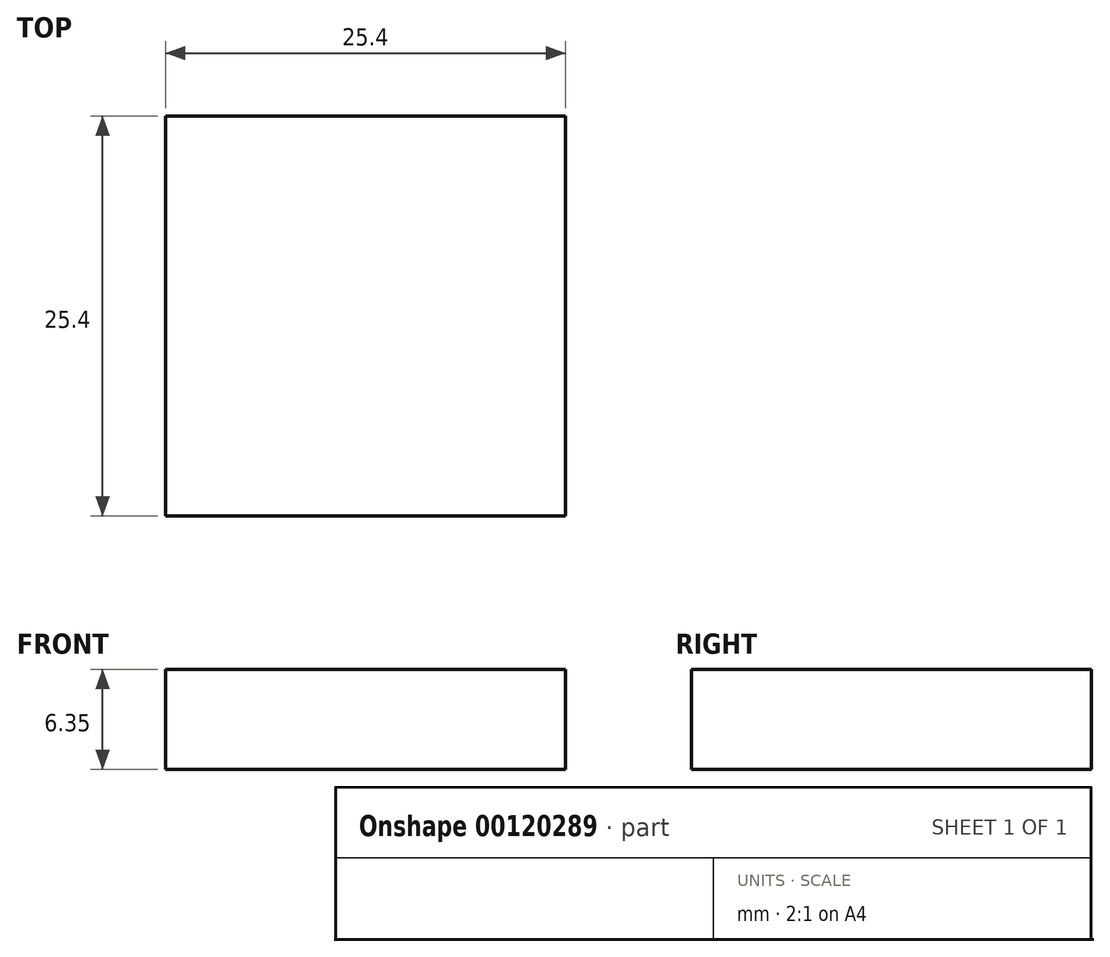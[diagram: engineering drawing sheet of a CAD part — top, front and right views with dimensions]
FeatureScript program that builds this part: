
annotation { "Feature Type Name" : "Feature", "Feature Type Description" : "" }
export const myFeature = defineFeature(function(context is Context, id is Id, definition is map)
    precondition{}
    {
        {
            var Q0;
            Q0=qCreatedBy(makeId("Top.planeOp"),FACE);
            var sketch = newSketch(context, id + "F0", { "sketchPlane" : qUnion([Q0])});
            skLineSegment(sketch, "E0.bottom", {"start": v(-12.7, 12.7) * mm, "end": v(12.7, 12.7) * mm});
            skLineSegment(sketch, "E0.top", {"start": v(-12.7, -12.7) * mm, "end": v(12.7, -12.7) * mm});
            skLineSegment(sketch, "E0.left", {"start": v(-12.7, 12.7) * mm, "end": v(-12.7, -12.7) * mm});
            skLineSegment(sketch, "E0.right", {"start": v(12.7, 12.7) * mm, "end": v(12.7, -12.7) * mm});
            skSolve(sketch);
        }
        {
            var Q0;
            Q0 = qSketchRegion(id + "F0", true);
            extrude(context, id + "F1", {"entities" : qUnion([Q0]), "depth" : 6.35 * mm});
        }
    });
